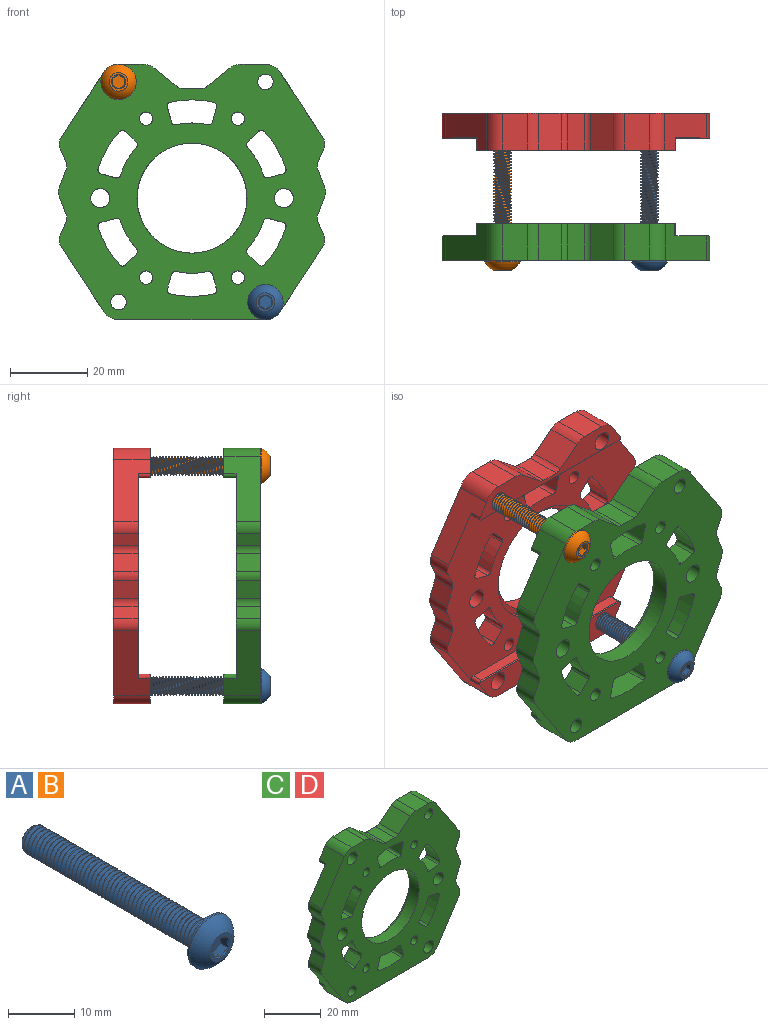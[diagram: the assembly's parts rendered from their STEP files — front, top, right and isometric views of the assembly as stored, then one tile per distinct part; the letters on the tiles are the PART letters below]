
ASSEMBLY  parts=4 mates=3
PART A: 24 faces, bbox 9.5x41.3x9.5 mm
  f0: cylinder r=2.41mm len=37.5mm, axis (0,1,0), area 70.6mm2, adj f2,f4,f6,f9
  f1: cone r=1.82mm half-angle=45deg, axis (0,-1,0), area 4.8mm2, adj f2,f3,f4,f5
  f2: cone r=1.82mm half-angle=45deg, axis (0,-1,0), area 1.3mm2, adj f0,f1,f4,f6
  f3: plane 3.64x3.64mm, normal (0,1,0), area 10.4mm2, adj f1
  f4: bspline ~38.7x4.83mm, area 383.1mm2, adj f0,f1,f2,f5,f9
  f5: cylinder r=1.9mm len=38.02mm, axis (0,-1,0), area 56.9mm2, adj f1,f4,f6,f9
  f6: bspline ~38.4x4.83mm, area 384.7mm2, adj f0,f2,f5,f9
  f7: sphere r=5.17mm, area 70.9mm2, adj f8,f10
  f8: plane 4.83x4.83mm, normal (0,-1,0), area 7.7mm2, adj f7,f11,f12,f13,f14,f15,f16
  f9: plane 9.48x9.48mm, normal (0,1,0), area 51.3mm2, adj f0,f4,f5,f6,f10
  f10: cylinder r=4.58mm len=9.17mm, axis (0,-1,0), area 11.1mm2, adj f7,f9
  f11: cone r=1.83mm half-angle=45deg, axis (0,-1,0), area 0.4mm2, adj f8,f18
  f12: cone r=1.83mm half-angle=45deg, axis (0,-1,0), area 0.4mm2, adj f8,f19
  f13: cone r=1.83mm half-angle=45deg, axis (0,-1,0), area 0.4mm2, adj f8,f20
  f14: cone r=1.83mm half-angle=45deg, axis (0,-1,0), area 0.4mm2, adj f8,f21
  f15: cone r=1.83mm half-angle=45deg, axis (0,-1,0), area 0.4mm2, adj f8,f22
  f16: cone r=1.83mm half-angle=45deg, axis (0,-1,0), area 0.4mm2, adj f8,f23
  f17: plane 3.67x3.18mm, normal (0,-1,0), area 8.7mm2, adj f18,f19,f20,f21,f22,f23
  f18: plane 1.84x1.8mm, normal (-1,0,0), area 3mm2, adj f11,f17,f19,f23
  f19: plane 1.8x1.59mm, normal (-0.5,0,-0.87), area 3mm2, adj f12,f17,f18,f20
  f20: plane 1.8x1.59mm, normal (0.5,0,-0.87), area 3mm2, adj f13,f17,f19,f21
  f21: plane 1.84x1.8mm, normal (1,0,0), area 3mm2, adj f14,f17,f20,f22
  f22: plane 1.8x1.59mm, normal (0.5,0,0.87), area 3mm2, adj f15,f17,f21,f23
  f23: plane 1.8x1.59mm, normal (-0.5,0,0.87), area 3mm2, adj f16,f17,f18,f22
PART B: same geometry as A
PART C: 111 faces, bbox 69.4x9.5x66.3 mm
  f0: cylinder r=15.88mm len=31.75mm, axis (0,1,0), area 164.7mm2, adj f97,f110
  f1: cylinder r=2.54mm len=6.35mm, axis (0,-1,0), area 12.9mm2, adj f35,f36,f50,f97
  f2: cylinder r=2.54mm len=6.35mm, axis (0,1,0), area 12.9mm2, adj f44,f45,f50,f97
  f3: cylinder r=2.49mm len=6.35mm, axis (0,-1,0), area 99.3mm2, adj f50,f97
  f4: cylinder r=2.49mm len=6.35mm, axis (0,-1,0), area 99.3mm2, adj f50,f97
  f5: cylinder r=0.79mm len=3.18mm, axis (0,-1,0), area 5.3mm2, adj f25,f43,f96,f97,f102
  f6: cylinder r=0.79mm len=3.18mm, axis (0,1,0), area 5.3mm2, adj f25,f39,f95,f97,f101
  f7: cylinder r=2.02mm len=9.53mm, axis (0,-1,0), area 120.8mm2, adj f50,f51
  f8: cylinder r=2.02mm len=9.53mm, axis (0,-1,0), area 120.8mm2, adj f25,f50
  f9: cylinder r=3.17mm len=6.35mm, axis (0,1,0), area 14.8mm2, adj f36,f37,f50,f97
  f10: cylinder r=3.17mm len=6.35mm, axis (0,-1,0), area 20.5mm2, adj f47,f48,f50,f97
  f11: cylinder r=3.17mm len=6.35mm, axis (0,-1,0), area 20.4mm2, adj f43,f44,f50,f97
  f12: cylinder r=1mm len=6.35mm, axis (0,-1,0), area 9.7mm2, adj f50,f87,f93,f97
  f13: cylinder r=1mm len=9.53mm, axis (0,-1,0), area 14.5mm2, adj f25,f50,f82,f83,f96,f97,f102
  f14: cylinder r=1mm len=6.35mm, axis (0,-1,0), area 10.2mm2, adj f50,f73,f79,f97
  f15: cylinder r=1mm len=6.35mm, axis (0,-1,0), area 10.2mm2, adj f50,f66,f67,f97
  f16: cylinder r=1mm len=6.35mm, axis (0,-1,0), area 10.2mm2, adj f50,f59,f60,f97
  f17: cylinder r=1mm len=6.35mm, axis (0,-1,0), area 9.7mm2, adj f50,f52,f58,f97
  f18: cylinder r=1.73mm len=6.35mm, axis (0,-1,0), area 68.9mm2, adj f50,f97
  f19: cylinder r=1.73mm len=6.35mm, axis (0,-1,0), area 68.9mm2, adj f50,f97
  f20: cylinder r=1.73mm len=6.35mm, axis (0,-1,0), area 68.9mm2, adj f50,f97
  f21: cylinder r=1.73mm len=6.35mm, axis (0,-1,0), area 68.9mm2, adj f50,f97
  f22: cylinder r=2.49mm len=9.53mm, axis (0,1,0), area 149mm2, adj f50,f51
  f23: cylinder r=2.49mm len=9.53mm, axis (0,1,0), area 149mm2, adj f25,f50
  f24: cylinder r=14.27mm len=28.55mm, axis (0,1,0), area 421.5mm2, adj f50,f110
  f25: plane 51.79x7.45mm, normal (0,1,0), area 308.4mm2, adj f5,f6,f8,f13,f23,f39,f40,f41
  f26: plane 9.53x6.35mm, normal (0,0,1), area 60.5mm2, adj f27,f49,f50,f51
  f27: cylinder r=4.58mm len=9.53mm, axis (0,1,0), area 29.5mm2, adj f26,f28,f50,f51
  f28: plane 9.53x5.96mm, normal (-0.63,0,0.78), area 72.8mm2, adj f27,f50,f51,f106
  f29: plane 9.53x4.56mm, normal (0,0,1), area 43.5mm2, adj f50,f51,f106,f107
  f30: plane 9.53x5.96mm, normal (0.63,0,0.78), area 72.8mm2, adj f31,f50,f51,f107
  f31: cylinder r=4.58mm len=9.53mm, axis (0,1,0), area 29.5mm2, adj f30,f32,f50,f51
  f32: plane 9.53x6.35mm, normal (0,0,1), area 60.5mm2, adj f31,f33,f50,f51
  f33: cylinder r=4.58mm len=9.53mm, axis (0,1,0), area 43.3mm2, adj f32,f34,f50,f51
  f34: plane 16.91x11.08mm, normal (-0.84,0,0.55), area 145.1mm2, adj f33,f50,f51,f97,f99,f104
  f35: plane 6.35x3.19mm, normal (-0.91,0,-0.42), area 22.3mm2, adj f1,f50,f97,f99
  f36: plane 6.35x4.8mm, normal (-0.93,0,0.36), area 32.6mm2, adj f1,f9,f50,f97
  f37: plane 6.35x4.8mm, normal (-0.93,0,-0.36), area 32.6mm2, adj f9,f50,f97,f109
  f38: plane 6.35x3.19mm, normal (-0.91,0,0.42), area 22.3mm2, adj f50,f97,f98,f109
  f39: plane 16.91x11.08mm, normal (-0.84,0,-0.55), area 145.1mm2, adj f6,f25,f40,f50,f97,f98
  f40: cylinder r=4.58mm len=9.53mm, axis (0,1,0), area 43.3mm2, adj f25,f39,f41,f50
  f41: plane 38.1x9.53mm, normal (0,0,-1), area 362.9mm2, adj f25,f40,f42,f50
  f42: cylinder r=4.58mm len=9.53mm, axis (0,1,0), area 43.3mm2, adj f25,f41,f43,f50
  f43: plane 16.91x11.08mm, normal (0.84,0,-0.55), area 145.1mm2, adj f5,f11,f25,f42,f50,f97
  f44: plane 6.35x3.19mm, normal (0.91,0,0.42), area 22.3mm2, adj f2,f11,f50,f97
  f45: plane 6.35x4.8mm, normal (0.93,0,-0.36), area 32.6mm2, adj f2,f50,f97,f100
  f46: plane 6.35x4.8mm, normal (0.93,0,0.36), area 32.6mm2, adj f50,f97,f100,f108
  f47: plane 6.35x3.19mm, normal (0.91,0,-0.42), area 22.3mm2, adj f10,f50,f97,f108
  f48: plane 16.04x10.62mm, normal (0.83,0,0.55), area 135.6mm2, adj f10,f49,f50,f51,f97,f105
  f49: cylinder r=4.58mm len=9.53mm, axis (0,1,0), area 52.6mm2, adj f26,f48,f50,f51
  f50: plane 69.4x66.32mm, normal (0,-1,0), area 2716.2mm2, adj f1,f2,f3,f4,f7,f8,f9,f10
  f51: plane 51.69x7.45mm, normal (0,1,0), area 230.8mm2, adj f7,f22,f26,f27,f28,f29,f30,f31
  f52: cylinder r=19.5mm len=7.2mm, axis (0,-1,0), area 53.2mm2, adj f17,f50,f53,f97
  f53: cylinder r=1mm len=6.35mm, axis (0,-1,0), area 9.7mm2, adj f50,f52,f54,f97
  f54: plane 6.35x3.87mm, normal (0.26,0,0.97), area 25.4mm2, adj f50,f53,f55,f97
  f55: cylinder r=1mm len=6.35mm, axis (0,-1,0), area 10.2mm2, adj f50,f54,f56,f97
  f56: cylinder r=25.5mm len=9.75mm, axis (0,-1,0), area 72.1mm2, adj f50,f55,f57,f97
  f57: cylinder r=1mm len=6.35mm, axis (0,-1,0), area 10.2mm2, adj f50,f56,f58,f97
  f58: plane 6.35x2.83mm, normal (-0.71,0,-0.71), area 25.4mm2, adj f17,f50,f57,f97
  f59: cylinder r=25.5mm len=11.26mm, axis (0,-1,0), area 72.1mm2, adj f16,f50,f65,f97
  f60: plane 6.35x3.87mm, normal (-0.97,0,0.26), area 25.4mm2, adj f16,f50,f61,f97
  f61: cylinder r=1mm len=6.35mm, axis (0,-1,0), area 9.7mm2, adj f50,f60,f62,f97
  f62: cylinder r=19.5mm len=8.32mm, axis (0,-1,0), area 53.2mm2, adj f50,f61,f63,f97
  f63: cylinder r=1mm len=6.35mm, axis (0,-1,0), area 9.7mm2, adj f50,f62,f64,f97
  f64: plane 6.35x3.87mm, normal (0.97,0,0.26), area 25.4mm2, adj f50,f63,f65,f97
  f65: cylinder r=1mm len=6.35mm, axis (0,-1,0), area 10.2mm2, adj f50,f59,f64,f97
  f66: cylinder r=25.5mm len=9.74mm, axis (0,-1,0), area 72.1mm2, adj f15,f50,f72,f97
  f67: plane 6.35x3.87mm, normal (-0.26,0,0.97), area 25.4mm2, adj f15,f50,f68,f97
  f68: cylinder r=1mm len=6.35mm, axis (0,-1,0), area 9.7mm2, adj f50,f67,f69,f97
  f69: cylinder r=19.5mm len=7.2mm, axis (0,-1,0), area 53.2mm2, adj f50,f68,f70,f97
  f70: cylinder r=1mm len=6.35mm, axis (0,-1,0), area 9.7mm2, adj f50,f69,f71,f97
  f71: plane 6.35x2.83mm, normal (0.71,0,-0.71), area 25.4mm2, adj f50,f70,f72,f97
  f72: cylinder r=1mm len=6.35mm, axis (0,-1,0), area 10.2mm2, adj f50,f66,f71,f97
  f73: cylinder r=25.5mm len=9.75mm, axis (0,-1,0), area 72.1mm2, adj f14,f50,f74,f97
  f74: cylinder r=1mm len=6.35mm, axis (0,-1,0), area 10.2mm2, adj f50,f73,f75,f97
  f75: plane 6.35x2.83mm, normal (0.71,0,0.71), area 25.4mm2, adj f50,f74,f76,f97
  f76: cylinder r=1mm len=6.35mm, axis (0,-1,0), area 9.7mm2, adj f50,f75,f77,f97
  f77: cylinder r=19.5mm len=7.2mm, axis (0,-1,0), area 53.2mm2, adj f50,f76,f78,f97
  f78: cylinder r=1mm len=6.35mm, axis (0,-1,0), area 9.7mm2, adj f50,f77,f79,f97
  f79: plane 6.35x3.87mm, normal (-0.26,0,-0.97), area 25.4mm2, adj f14,f50,f78,f97
  f80: cylinder r=19.5mm len=8.32mm, axis (0,-1,0), area 53.2mm2, adj f50,f81,f86,f97
  f81: cylinder r=1mm len=6.35mm, axis (0,-1,0), area 9.7mm2, adj f50,f80,f82,f97
  f82: plane 6.35x3.87mm, normal (-0.97,0,-0.26), area 25.4mm2, adj f13,f50,f81,f97
  f83: cylinder r=25.5mm len=11.26mm, axis (0,-1,0), area 108.1mm2, adj f13,f25,f50,f84
  f84: cylinder r=1mm len=9.53mm, axis (0,-1,0), area 14.6mm2, adj f25,f50,f83,f85,f95,f97,f101
  f85: plane 6.35x3.87mm, normal (0.97,0,-0.26), area 25.4mm2, adj f50,f84,f86,f97
  f86: cylinder r=1mm len=6.35mm, axis (0,-1,0), area 9.7mm2, adj f50,f80,f85,f97
  f87: plane 6.35x2.83mm, normal (-0.71,0,0.71), area 25.4mm2, adj f12,f50,f88,f97
  f88: cylinder r=1mm len=6.35mm, axis (0,-1,0), area 10.2mm2, adj f50,f87,f89,f97
  f89: cylinder r=25.5mm len=9.74mm, axis (0,-1,0), area 72.1mm2, adj f50,f88,f90,f97
  f90: cylinder r=1mm len=6.35mm, axis (0,-1,0), area 10.2mm2, adj f50,f89,f91,f97
  f91: plane 6.35x3.87mm, normal (0.26,0,-0.97), area 25.4mm2, adj f50,f90,f92,f97
  f92: cylinder r=1mm len=6.35mm, axis (0,-1,0), area 9.7mm2, adj f50,f91,f93,f97
  f93: cylinder r=19.5mm len=7.2mm, axis (0,-1,0), area 53.2mm2, adj f12,f50,f92,f97
  f94: plane 50.1x2.93mm, normal (0,0,-1), area 146.5mm2, adj f97,f103,f104,f105
  f95: plane 18.7x2.93mm, normal (0,0,1), area 54.7mm2, adj f6,f84,f97,f101
  f96: plane 18.68x2.93mm, normal (0,0,1), area 54.6mm2, adj f5,f13,f97,f102
  f97: plane 69.4x53.39mm, normal (0,1,0), area 2003.2mm2, adj f0,f1,f2,f3,f4,f5,f6,f9
  f98: cylinder r=3.17mm len=6.35mm, axis (0,-1,0), area 20.4mm2, adj f38,f39,f50,f97
  f99: cylinder r=3.17mm len=6.35mm, axis (0,-1,0), area 20.4mm2, adj f34,f35,f50,f97
  f100: cylinder r=3.17mm len=6.35mm, axis (0,1,0), area 14.8mm2, adj f45,f46,f50,f97
  f101: plane 19.31x0.25mm, normal (0,0.71,0.71), area 6.8mm2, adj f6,f25,f84,f95
  f102: plane 19.29x0.25mm, normal (0,0.71,0.71), area 6.7mm2, adj f5,f13,f25,f96
  f103: plane 51.26x0.25mm, normal (0,0.71,-0.71), area 18mm2, adj f51,f94,f104,f105
  f104: cylinder r=0.79mm len=3.18mm, axis (0,-1,0), area 5.3mm2, adj f34,f51,f94,f97,f103
  f105: cylinder r=0.79mm len=3.18mm, axis (0,1,0), area 5.3mm2, adj f48,f51,f94,f97,f103
  f106: cylinder r=2.54mm len=9.53mm, axis (0,-1,0), area 16.4mm2, adj f28,f29,f50,f51
  f107: cylinder r=2.54mm len=9.53mm, axis (0,-1,0), area 16.4mm2, adj f29,f30,f50,f51
  f108: cylinder r=2.54mm len=6.35mm, axis (0,-1,0), area 12.9mm2, adj f46,f47,f50,f97
  f109: cylinder r=2.54mm len=6.35mm, axis (0,1,0), area 12.9mm2, adj f37,f38,f50,f97
  f110: plane 31.75x31.75mm, normal (0,1,0), area 151.6mm2, adj f0,f24
PART D: same geometry as C
PLACE A t=(-31.02,-28.72,-17.3)mm
PLACE B t=(-69.12,-28.72,39.85)mm
PLACE C t=(-50.07,-21.39,11.28)mm fixed
PLACE D rot(axis=(0,0,1),180deg) t=(-50.07,7.19,11.28)mm
MATE fastened B.f10 <-> C.f22  axis (0,1,0) through (-69.12,-26.15,39.85)mm
MATE fastened A.f10 <-> C.f23  axis (0,1,0) through (-31.02,-26.15,-17.3)mm
MATE fastened C.f0 <-> D.f0  axis (0,-1,0) through (-50.07,-26.15,9.69)mm
